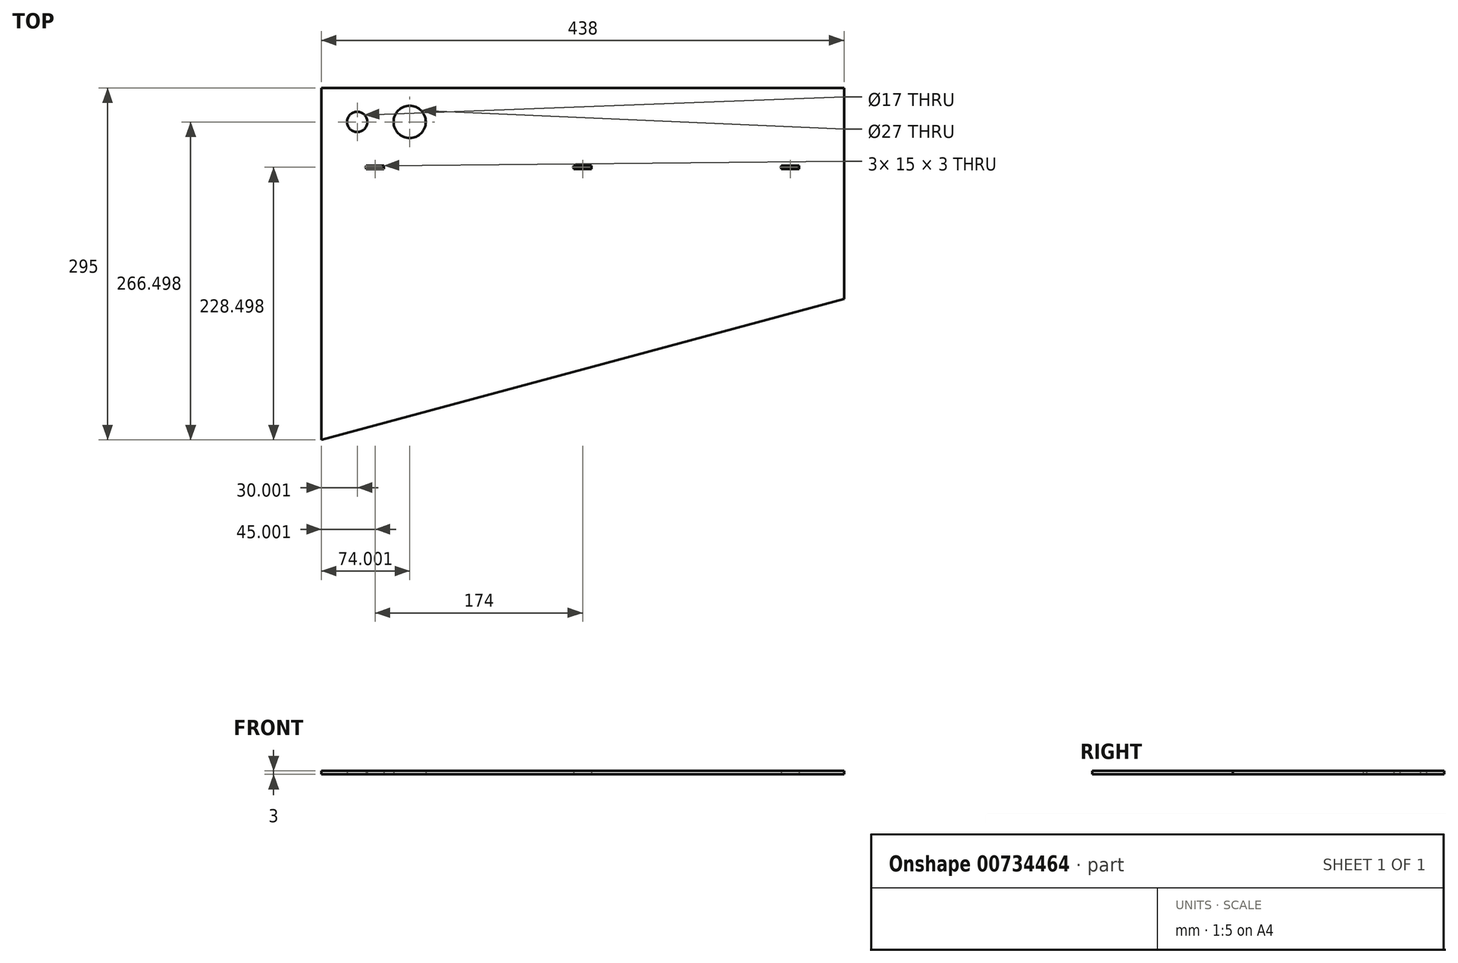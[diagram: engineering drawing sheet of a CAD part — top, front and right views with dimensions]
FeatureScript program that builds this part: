
annotation { "Feature Type Name" : "Feature", "Feature Type Description" : "" }
export const myFeature = defineFeature(function(context is Context, id is Id, definition is map)
    precondition{}
    {
        {
            var Q0;
            Q0=qCreatedBy(makeId("Top.planeOp"),FACE);
            var sketch = newSketch(context, id + "F0", { "sketchPlane" : qUnion([Q0])});
            skLineSegment(sketch, "E0", {"start": v(-185.79, 212.46) * mm, "end": v(-185.79, -82.54) * mm});
            skLineSegment(sketch, "E1", {"start": v(-185.79, 212.46) * mm, "end": v(252.21, 212.46) * mm});
            skLineSegment(sketch, "E2", {"start": v(252.21, 212.46) * mm, "end": v(252.21, 35.46) * mm});
            skLineSegment(sketch, "E3", {"start": v(252.21, 35.46) * mm, "end": v(-185.79, -82.54) * mm});
            skCircle(sketch, "E4", {"center": v(-155.79, 183.96) * mm, "radius": 8.5 * mm});
            skCircle(sketch, "E5", {"center": v(-111.79, 183.96) * mm, "radius": 13.5 * mm});
            skLineSegment(sketch, "E6.bottom", {"start": v(-148.29, 144.46) * mm, "end": v(-133.29, 144.46) * mm});
            skLineSegment(sketch, "E6.top", {"start": v(-148.29, 147.46) * mm, "end": v(-133.29, 147.46) * mm});
            skLineSegment(sketch, "E6.left", {"start": v(-148.29, 144.46) * mm, "end": v(-148.29, 147.46) * mm});
            skLineSegment(sketch, "E6.right", {"start": v(214.71, 144.46) * mm, "end": v(214.71, 147.46) * mm});
            skLineSegment(sketch, "E7.left", {"start": v(-148.29, 147.46) * mm, "end": v(-148.29, 144.46) * mm});
            skLineSegment(sketch, "E7.right", {"start": v(-133.29, 147.46) * mm, "end": v(-133.29, 144.46) * mm});
            skLineSegment(sketch, "E8.bottom", {"start": v(214.71, 147.46) * mm, "end": v(199.71, 147.46) * mm});
            skLineSegment(sketch, "E8.top", {"start": v(214.71, 144.46) * mm, "end": v(199.71, 144.46) * mm});
            skLineSegment(sketch, "E8.left", {"start": v(214.71, 147.46) * mm, "end": v(214.71, 144.46) * mm});
            skLineSegment(sketch, "E8.right", {"start": v(199.71, 147.46) * mm, "end": v(199.71, 144.46) * mm});
            skLineSegment(sketch, "E9.bottom", {"start": v(25.71, 147.46) * mm, "end": v(40.71, 147.46) * mm});
            skLineSegment(sketch, "E9.top", {"start": v(25.71, 144.46) * mm, "end": v(40.71, 144.46) * mm});
            skLineSegment(sketch, "E9.left", {"start": v(25.71, 147.46) * mm, "end": v(25.71, 144.46) * mm});
            skLineSegment(sketch, "E9.right", {"start": v(40.71, 147.46) * mm, "end": v(40.71, 144.46) * mm});
            skLineSegment(sketch, "E10.trimOffspring", {"start": v(199.71, 144.46) * mm, "end": v(214.71, 144.46) * mm});
            skLineSegment(sketch, "E11.trimOffspring", {"start": v(199.71, 147.46) * mm, "end": v(214.71, 147.46) * mm});
            skSolve(sketch);
        }
        {
            var Q0;
            Q0=makeQuery(id+"F0.imprint","IMPRINT",FACE,{"disambiguationData":[TD([[makeQuery(id+"F0.imprint","IMPRINT",EDGE,{"derivedFrom":sQuery(id+"F0.wireOp",EDGE,"E0")}),1.0]])]});
            extrude(context, id + "F1", {"entities" : qUnion([Q0]), "depth" : 3 * mm});
        }
    });
